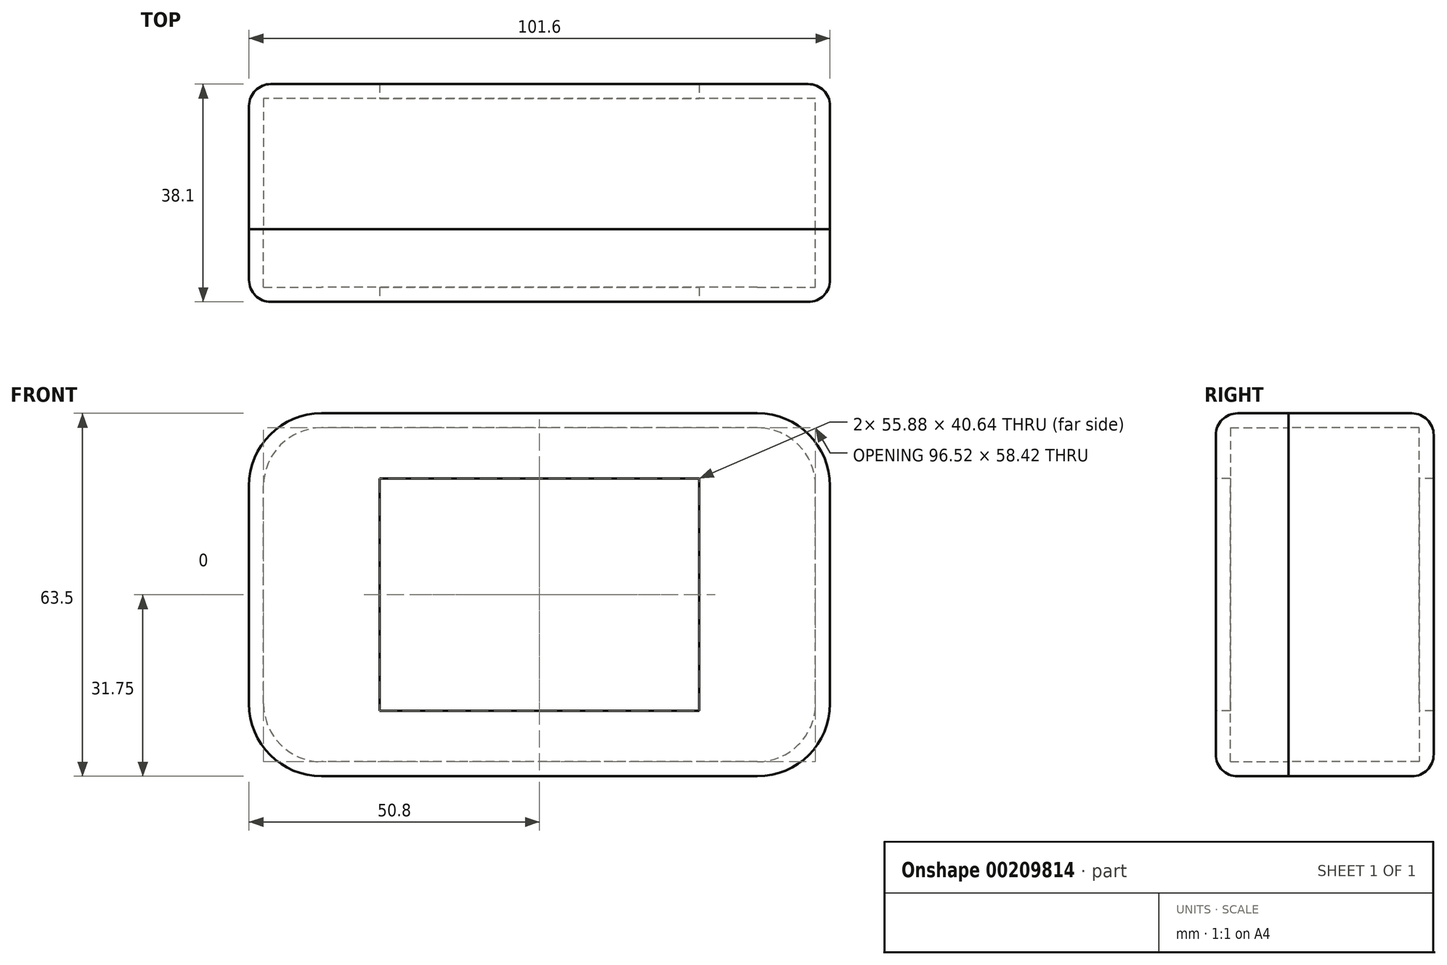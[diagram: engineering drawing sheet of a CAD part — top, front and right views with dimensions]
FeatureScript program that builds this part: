
annotation { "Feature Type Name" : "Feature", "Feature Type Description" : "" }
export const myFeature = defineFeature(function(context is Context, id is Id, definition is map)
    precondition{}
    {
        {
            var Q0;
            Q0=qCreatedBy(makeId("Front.planeOp"),FACE);
            var sketch = newSketch(context, id + "F0", { "sketchPlane" : qUnion([Q0])});
            skLineSegment(sketch, "E0.bottom", {"start": v(38.1, -31.75) * mm, "end": v(-38.1, -31.75) * mm});
            skLineSegment(sketch, "E0.top", {"start": v(38.1, 31.75) * mm, "end": v(-38.1, 31.75) * mm});
            skLineSegment(sketch, "E0.left", {"start": v(50.8, -19.05) * mm, "end": v(50.8, 19.05) * mm});
            skLineSegment(sketch, "E0.right", {"start": v(-50.8, -19.05) * mm, "end": v(-50.8, 19.05) * mm});
            skPoint(sketch, "E0.middle", {"position": v(0, 0) * mm});
            skPoint(sketch, "E1.visualSharp", {"position": v(-50.8, 31.75) * mm});
            skArc(sketch, "E1.filletArc", {"start": v(-38.1, 31.75) * mm, "mid": v(-47.08, 28.03) * mm, "end": v(-50.8, 19.05) * mm});
            skPoint(sketch, "E2.visualSharp", {"position": v(50.8, 31.75) * mm});
            skArc(sketch, "E2.filletArc", {"start": v(50.8, 19.05) * mm, "mid": v(47.08, 28.03) * mm, "end": v(38.1, 31.75) * mm});
            skPoint(sketch, "E3.visualSharp", {"position": v(50.8, -31.75) * mm});
            skArc(sketch, "E3.filletArc", {"start": v(38.1, -31.75) * mm, "mid": v(47.08, -28.03) * mm, "end": v(50.8, -19.05) * mm});
            skPoint(sketch, "E4.visualSharp", {"position": v(-50.8, -31.75) * mm});
            skArc(sketch, "E4.filletArc", {"start": v(-50.8, -19.05) * mm, "mid": v(-47.08, -28.03) * mm, "end": v(-38.1, -31.75) * mm});
            skSolve(sketch);
        }
        {
            var Q0;
            Q0 = qSketchRegion(id + "F0", true);
            extrude(context, id + "F1", {"entities" : qUnion([Q0]), "depth" : 12.7 * mm});
        }
        {
            var Q0;
            Q0=makeQuery(id+"F1.opExtrude","CAP_FACE",FACE,{"disambiguationData":[OSD([sQuery(id+"F0.wireOp",EDGE,"E0.bottom"),sQuery(id+"F0.wireOp",EDGE,"E0.top"),sQuery(id+"F0.wireOp",EDGE,"E0.left"),sQuery(id+"F0.wireOp",EDGE,"E0.right")])],"isStart":false});
            var sketch = newSketch(context, id + "F2", { "sketchPlane" : qUnion([Q0])});
            skLineSegment(sketch, "E5.bottom", {"start": v(-27.94, 20.32) * mm, "end": v(27.94, 20.32) * mm});
            skLineSegment(sketch, "E5.top", {"start": v(-27.94, -20.32) * mm, "end": v(27.94, -20.32) * mm});
            skLineSegment(sketch, "E5.left", {"start": v(-27.94, 20.32) * mm, "end": v(-27.94, -20.32) * mm});
            skLineSegment(sketch, "E5.right", {"start": v(27.94, 20.32) * mm, "end": v(27.94, -20.32) * mm});
            skLineSegment(sketch, "E6", {"start": v(0, 31.75) * mm, "end": v(0, -31.75) * mm, "construction": true});
            skLineSegment(sketch, "E7", {"start": v(-50.8, 0) * mm, "end": v(50.8, 0) * mm, "construction": true});
            skSolve(sketch);
        }
        {
            var Q0;
            Q0 = qSketchRegion(id + "F0", true);
            extrude(context, id + "F3", {"entities" : qUnion([Q0]), "oppositeDirection" : true, "depth" : 25.4 * mm});
        }
        {
            var Q0;
            Q0=makeQuery(id+"F1.opExtrude","CAP_FACE",FACE,{"disambiguationData":[OSD([sQuery(id+"F0.wireOp",EDGE,"E0.bottom"),sQuery(id+"F0.wireOp",EDGE,"E0.top"),sQuery(id+"F0.wireOp",EDGE,"E0.left"),sQuery(id+"F0.wireOp",EDGE,"E0.right"),sQuery(id+"F0.wireOp",EDGE,"E1.filletArc"),sQuery(id+"F0.wireOp",EDGE,"E2.filletArc"),sQuery(id+"F0.wireOp",EDGE,"E3.filletArc"),sQuery(id+"F0.wireOp",EDGE,"E4.filletArc")])],"isStart":true});
            var Q1;
            Q1=makeQuery(id+"F3.opExtrude","CAP_FACE",FACE,{"disambiguationData":[OSD([sQuery(id+"F0.wireOp",EDGE,"E0.bottom"),sQuery(id+"F0.wireOp",EDGE,"E0.top"),sQuery(id+"F0.wireOp",EDGE,"E0.left"),sQuery(id+"F0.wireOp",EDGE,"E0.right"),sQuery(id+"F0.wireOp",EDGE,"E1.filletArc"),sQuery(id+"F0.wireOp",EDGE,"E2.filletArc"),sQuery(id+"F0.wireOp",EDGE,"E3.filletArc"),sQuery(id+"F0.wireOp",EDGE,"E4.filletArc")])],"isStart":true});
            shell(context, id + "F4", {"entities" : qUnion([Q0, Q1]), "thickness" : 2.54 * mm});
        }
        {
            var Q0;
            Q0 = qSketchRegion(id + "F2", true);
            extrude(context, id + "F5", {"entities" : qUnion([Q0]), "operationType" : NewBodyOperationType.REMOVE, "endBound" : BoundingType.THROUGH_ALL, "oppositeDirection" : true, "depth" : 25.4 * mm});
        }
        {
            var Q0;
            Q0=makeQuery(id+"F1.opExtrude","CAP_EDGE",EDGE,{"disambiguationData":[OSD([sQuery(id+"F0.wireOp",EDGE,"E0.top")])],"isStart":false});
            var Q1;
            Q1=makeQuery(id+"F3.opExtrude","CAP_EDGE",EDGE,{"disambiguationData":[OSD([sQuery(id+"F0.wireOp",EDGE,"E0.top")])],"isStart":false});
            fillet(context, id + "F6", {"entities" : qUnion([Q0, Q1]), "radius" : 3.8 * mm, "tangentPropagation" : true, "allowEdgeOverflow" : false});
        }
    });
